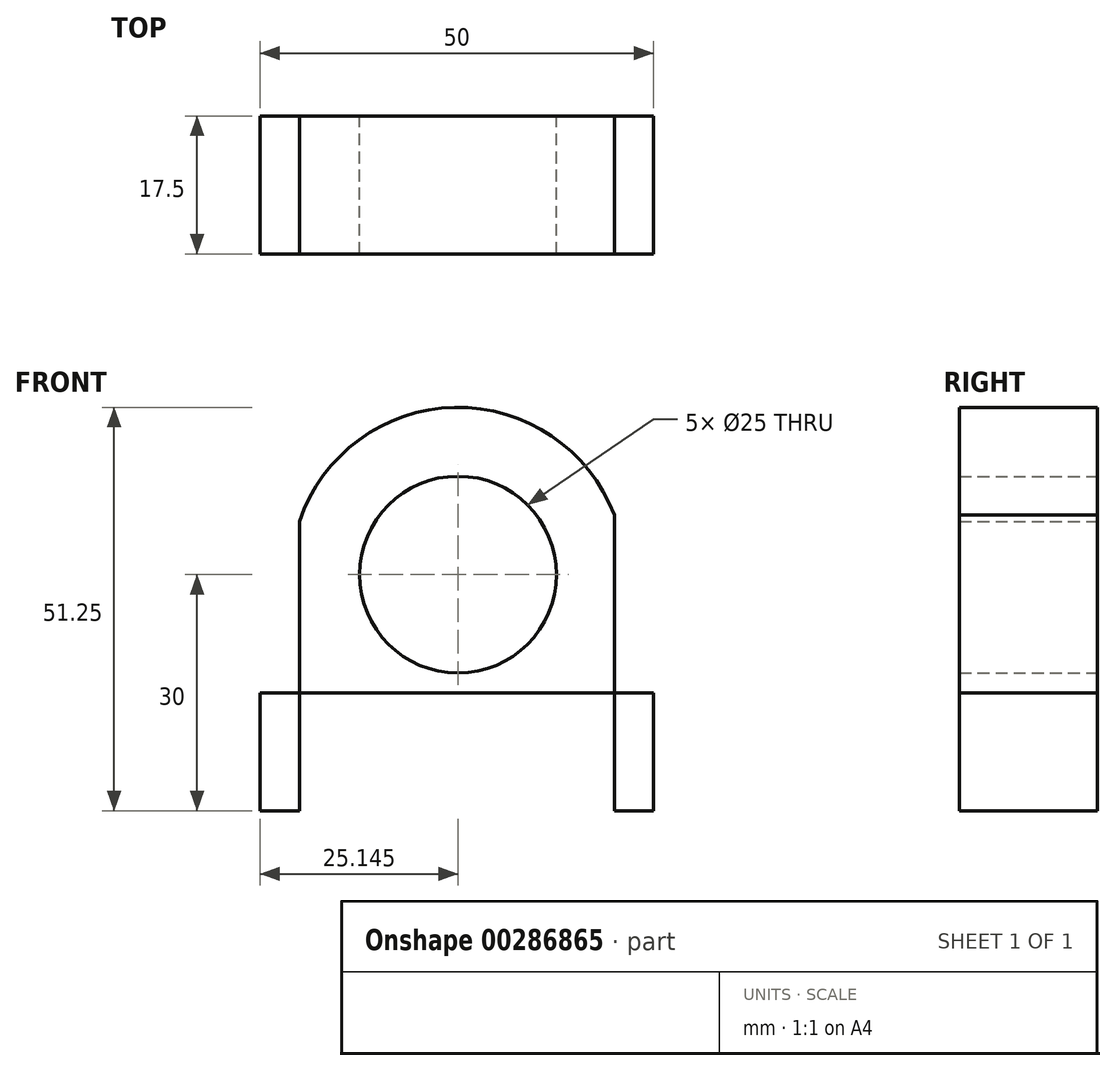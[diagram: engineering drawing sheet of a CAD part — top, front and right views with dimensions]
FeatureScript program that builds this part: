
annotation { "Feature Type Name" : "Feature", "Feature Type Description" : "" }
export const myFeature = defineFeature(function(context is Context, id is Id, definition is map)
    precondition{}
    {
        {
            var Q0;
            Q0=qCreatedBy(makeId("Front.planeOp"),FACE);
            var sketch = newSketch(context, id + "F0", { "sketchPlane" : qUnion([Q0])});
            skLineSegment(sketch, "E0", {"start": v(0, 0) * mm, "end": v(-5, 0) * mm});
            skLineSegment(sketch, "E1", {"start": v(-5, 0) * mm, "end": v(-5, 15) * mm});
            skLineSegment(sketch, "E2", {"start": v(-5, 15) * mm, "end": v(-45, 15) * mm});
            skLineSegment(sketch, "E3", {"start": v(-45, 15) * mm, "end": v(-45, 0) * mm});
            skLineSegment(sketch, "E4", {"start": v(-45, 0) * mm, "end": v(-50, 0) * mm});
            skLineSegment(sketch, "E5", {"start": v(-50, 0) * mm, "end": v(-50, 15) * mm});
            skLineSegment(sketch, "E6", {"start": v(-50, 15) * mm, "end": v(-45, 15) * mm});
            skLineSegment(sketch, "E7", {"start": v(-45, 15) * mm, "end": v(-45, 36.76) * mm});
            skLineSegment(sketch, "E8", {"start": v(-5, 37.57) * mm, "end": v(-5, 15) * mm});
            skLineSegment(sketch, "E9", {"start": v(-5, 15) * mm, "end": v(0, 15) * mm});
            skLineSegment(sketch, "E10", {"start": v(0, 15) * mm, "end": v(0, 0) * mm});
            skArc(sketch, "E11", {"start": v(-5, 37.57) * mm, "mid": v(-25.29, 51.25) * mm, "end": v(-45, 36.76) * mm});
            skCircle(sketch, "E12", {"center": v(-24.85, 30) * mm, "radius": 12.5 * mm});
            skSolve(sketch);
        }
        {
            var Q0;
            Q0 = qSketchRegion(id + "F0", true);
            extrude(context, id + "F1", {"entities" : qUnion([Q0]), "depth" : 17.5 * mm});
        }
    });
